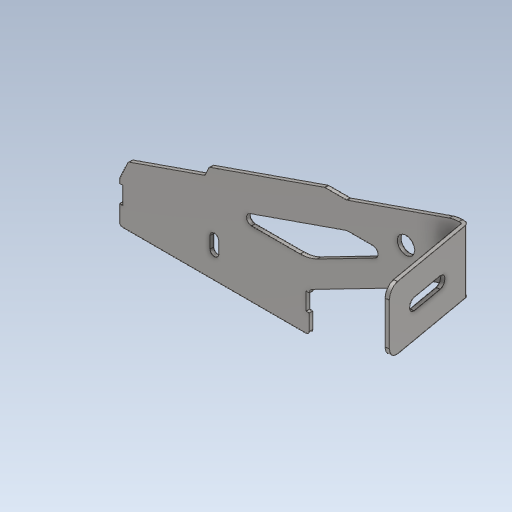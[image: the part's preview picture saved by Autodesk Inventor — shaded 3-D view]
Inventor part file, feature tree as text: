
AUTODESK INVENTOR PART (.ipt)
format: ipt  version: 2020 (Build 240168000, 168)  size: 221,696 bytes
history: native  units: mm
features: other x4, sketch x1, plane x1
ambient origin geometry x8: Origin, YZ Plane, XZ Plane, XY Plane, X Axis, Y Axis, Z Axis, Center Point
bodies: Body1 (feature_tree)
feature tree (6):
  other  "吊架-短(R)(#11.02).ipt"
  other  "實體1::吊架-短(R)(#11.02).ipt"
  other  "標籤特徵1"
  sketch  "草圖1"
  plane  "工作平面1"
  other  "實體1"
